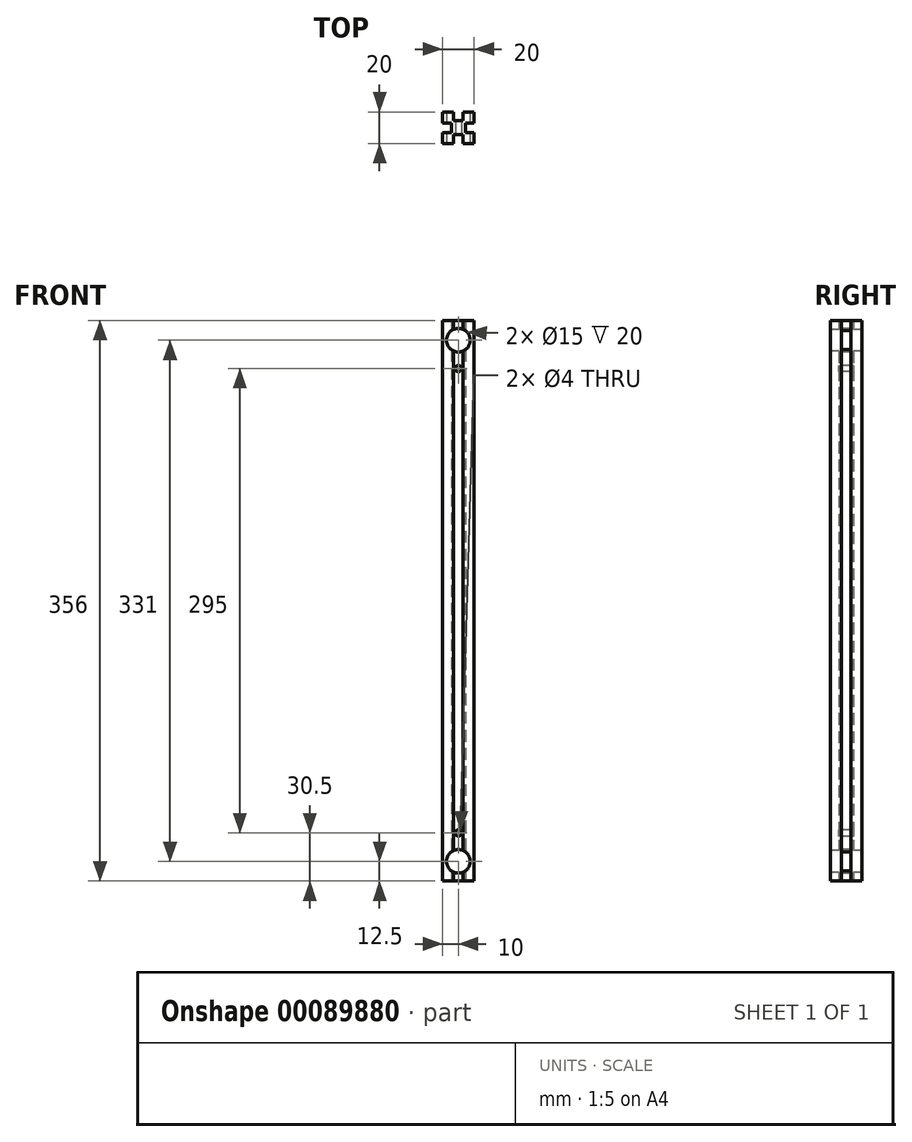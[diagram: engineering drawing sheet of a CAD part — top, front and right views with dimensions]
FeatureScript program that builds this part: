
annotation { "Feature Type Name" : "Feature", "Feature Type Description" : "" }
export const myFeature = defineFeature(function(context is Context, id is Id, definition is map)
    precondition{}
    {
        {
            var Q0;
            Q0=qCreatedBy(makeId("Top.planeOp"),FACE);
            var sketch = newSketch(context, id + "F0", { "sketchPlane" : qUnion([Q0])});
            skLineSegment(sketch, "E0.bottom", {"start": v(0, 0) * mm, "end": v(20, 0) * mm});
            skLineSegment(sketch, "E0.top", {"start": v(0, 20) * mm, "end": v(20, 20) * mm});
            skLineSegment(sketch, "E0.left", {"start": v(0, 0) * mm, "end": v(0, 20) * mm});
            skLineSegment(sketch, "E0.right", {"start": v(20, 0) * mm, "end": v(20, 20) * mm});
            skLineSegment(sketch, "E1.bottom", {"start": v(7, 20) * mm, "end": v(13, 20) * mm});
            skLineSegment(sketch, "E1.top", {"start": v(7, 14.5) * mm, "end": v(13, 14.5) * mm});
            skLineSegment(sketch, "E1.left", {"start": v(7, 20) * mm, "end": v(7, 14.5) * mm});
            skLineSegment(sketch, "E1.right", {"start": v(13, 20) * mm, "end": v(13, 14.5) * mm});
            skLineSegment(sketch, "E2.bottom", {"start": v(20, 13) * mm, "end": v(14.5, 13) * mm});
            skLineSegment(sketch, "E2.top", {"start": v(20, 7) * mm, "end": v(14.5, 7) * mm});
            skLineSegment(sketch, "E2.left", {"start": v(20, 13) * mm, "end": v(20, 7) * mm});
            skLineSegment(sketch, "E2.right", {"start": v(14.5, 13) * mm, "end": v(14.5, 7) * mm});
            skLineSegment(sketch, "E3.bottom", {"start": v(13, 0) * mm, "end": v(7, 0) * mm});
            skLineSegment(sketch, "E3.top", {"start": v(13, 5.5) * mm, "end": v(7, 5.5) * mm});
            skLineSegment(sketch, "E3.left", {"start": v(13, 0) * mm, "end": v(13, 5.5) * mm});
            skLineSegment(sketch, "E3.right", {"start": v(7, 0) * mm, "end": v(7, 5.5) * mm});
            skLineSegment(sketch, "E4.bottom", {"start": v(0, 7) * mm, "end": v(5.5, 7) * mm});
            skLineSegment(sketch, "E4.top", {"start": v(0, 13) * mm, "end": v(5.5, 13) * mm});
            skLineSegment(sketch, "E4.left", {"start": v(0, 7) * mm, "end": v(0, 13) * mm});
            skLineSegment(sketch, "E4.right", {"start": v(5.5, 7) * mm, "end": v(5.5, 13) * mm});
            skSolve(sketch);
        }
        {
            var Q0;
            Q0=makeQuery(id+"F0.imprint","IMPRINT",FACE,{"disambiguationData":[TD([[makeQuery(id+"F0.imprint","IMPRINT",EDGE,{"derivedFrom":sQuery(id+"F0.wireOp",EDGE,"E1.top")}),-1.0]])]});
            extrude(context, id + "F1", {"entities" : qUnion([Q0]), "depth" : 356 * mm});
        }
        {
            var Q0;
            {var subQ0=sQuery(id+"F0.wireOp",EDGE,"E0.bottom");Q0=makeQuery(id+"F1.opExtrude","SWEPT_FACE",FACE,{"disambiguationData":[OSD([subQ0]),TDD([makeQuery(id+"F0.imprint","IMPRINT",EDGE,{"disambiguationData":[TD([[makeQuery(id+"F0.imprint","INTERSECT",VERTEX,{"derivedFrom":[subQ0,sQuery(id+"F0.wireOp",EDGE,"E0.left")]}),-1.0]])],"derivedFrom":subQ0})])]});}
            var sketch = newSketch(context, id + "F2", { "sketchPlane" : qUnion([Q0])});
            skCircle(sketch, "E5", {"center": v(10, 343.5) * mm, "radius": 7.5 * mm});
            skCircle(sketch, "E6", {"center": v(10, 12.5) * mm, "radius": 7.5 * mm});
            skCircle(sketch, "E7", {"center": v(10, 325.5) * mm, "radius": 2 * mm});
            skCircle(sketch, "E8", {"center": v(10, 30.5) * mm, "radius": 2 * mm});
            skLineSegment(sketch, "E9", {"start": v(10, 325.5) * mm, "end": v(10, 336) * mm});
            skLineSegment(sketch, "E10", {"start": v(10, 30.5) * mm, "end": v(10, 20) * mm});
            skSolve(sketch);
        }
        {
            var Q0;
            Q0=qSketchRegion(id+"F2",true);
            extrude(context, id + "F3", {"entities" : qUnion([Q0]), "operationType" : NewBodyOperationType.REMOVE, "oppositeDirection" : true, "depth" : 25 * mm});
        }
    });
